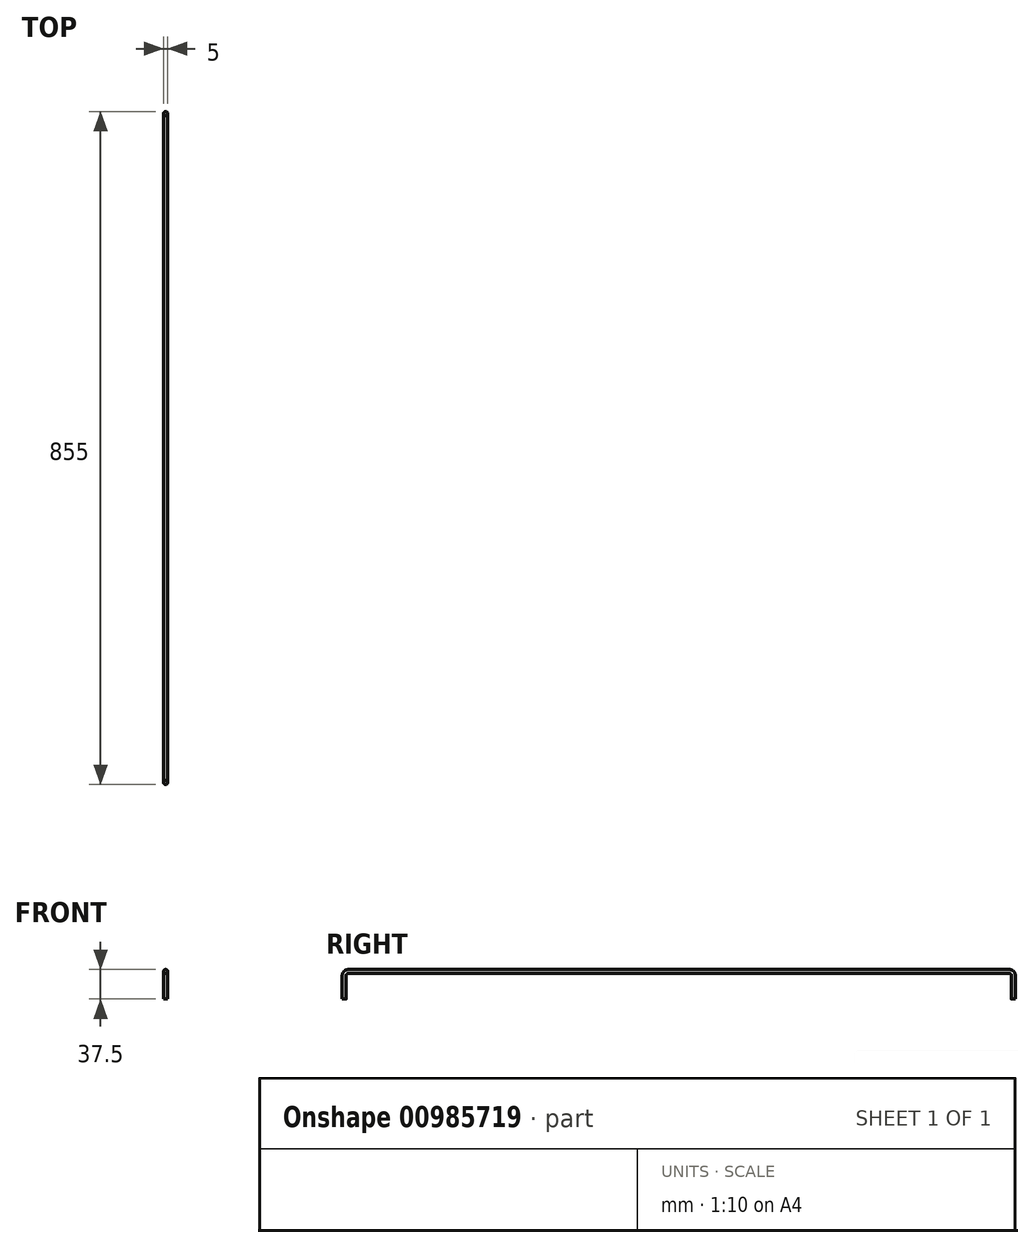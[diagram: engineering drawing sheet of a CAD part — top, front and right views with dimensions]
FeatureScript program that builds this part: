
annotation { "Feature Type Name" : "Feature", "Feature Type Description" : "" }
export const myFeature = defineFeature(function(context is Context, id is Id, definition is map)
    precondition{}
    {
        {
            var Q0;
            Q0=qCreatedBy(makeId("Right.planeOp"),FACE);
            var sketch = newSketch(context, id + "F0", { "sketchPlane" : qUnion([Q0])});
            skLineSegment(sketch, "E0", {"start": v(0, 0) * mm, "end": v(0, 30) * mm});
            skLineSegment(sketch, "E1", {"start": v(5, 35) * mm, "end": v(845, 35) * mm});
            skLineSegment(sketch, "E2", {"start": v(850, 30) * mm, "end": v(850, 0) * mm});
            skPoint(sketch, "E3.visualSharp", {"position": v(0, 35) * mm});
            skArc(sketch, "E3.filletArc", {"start": v(5, 35) * mm, "mid": v(1.46, 33.54) * mm, "end": v(0, 30) * mm});
            skPoint(sketch, "E4.visualSharp", {"position": v(850, 35) * mm});
            skArc(sketch, "E4.filletArc", {"start": v(850, 30) * mm, "mid": v(848.54, 33.54) * mm, "end": v(845, 35) * mm});
            skSolve(sketch);
        }
        {
            var Q0;
            Q0=qCreatedBy(makeId("Top.planeOp"),FACE);
            var sketch = newSketch(context, id + "F1", { "sketchPlane" : qUnion([Q0])});
            skCircle(sketch, "E5", {"center": v(0, 0) * mm, "radius": 2.5 * mm});
            skSolve(sketch);
        }
        {
            var Q0;
            Q0=makeQuery(id+"F1.imprint","IMPRINT",FACE,{"disambiguationData":[TD([[makeQuery(id+"F1.imprint","IMPRINT",EDGE,{"derivedFrom":sQuery(id+"F1.wireOp",EDGE,"E5")}),1.0]])]});
            var Q1;
            Q1=sQuery(id+"F0.wireOp",EDGE,"E0");
            var Q2;
            Q2=sQuery(id+"F0.wireOp",EDGE,"E3.filletArc");
            var Q3;
            Q3=sQuery(id+"F0.wireOp",EDGE,"E1");
            var Q4;
            Q4=sQuery(id+"F0.wireOp",EDGE,"E4.filletArc");
            var Q5;
            Q5=sQuery(id+"F0.wireOp",EDGE,"E2");
            sweep(context, id + "F2", {"profiles" : qUnion([Q0]), "path" : qUnion([Q1, Q2, Q3, Q4, Q5])});
        }
    });
